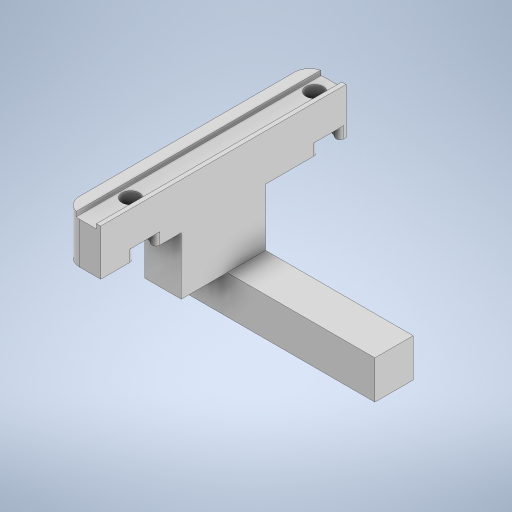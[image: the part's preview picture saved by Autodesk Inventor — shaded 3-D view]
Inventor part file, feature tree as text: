
AUTODESK INVENTOR PART (.ipt)
format: ipt  version: 2024 (Build 280153000, 153)  size: 317,952 bytes
history: native  units: in
note: dims shown in document units (in); Inventor stores cm internally (conversion verified against a paired STEP export)
features: extrude x5, sketch x5, projected_geometry x4, fillet x2
ambient origin geometry x8: Origin, YZ Plane, XZ Plane, XY Plane, X Axis, Y Axis, Z Axis, Center Point
bodies: Solid1 (feature_tree)
feature tree (16):
  extrude  "Extrusion1"  Depth=2.5197in
  extrude  "Extrusion2"  Depth=1.8898in
  extrude  "Extrusion3"  Depth=0.4724in TaperAngle=0.0deg
  fillet  "Fillet1"  Radius=0.0433in
  fillet  "Fillet2"  Radius=0.2126in
  extrude  "Extrusion15"  Depth=0.4724in TaperAngle=0.0deg
  extrude  "Extrusion18"  Depth=0.1181in TaperAngle=0.0deg
  sketch  "Sketch1"  dims[d1=0.374in d2=2.5197in]
  sketch  "Sketch2"  dims[d3=0.1772in d4=1.8898in]
  sketch  "Sketch3"  dims[d6=0.1457in d7=0.4724in d8=0.0in d9=0.0433in d10=0.2126in]
  projected_geometry  "Projected Loop2"
  projected_geometry  "Projected Loop3"
  projected_geometry  "Projected Loop4"
  projected_geometry  "Projected Loop5"
  sketch  "Sketch15"  dims[d11=0.0472in d12=0.4724in d13=0.0in]
  sketch  "Sketch27"  dims[d14=0.2953in d15=0.1181in d16=0.0in d17=0.1772in d18=0.0394in d19=0.1575in d76=0.4724in d79=0.4331in d80=0.8661in d81=0.5906in d82=0.0in d101=1.8898in d102=0.3937in d103=2.3622in d104=0.3937in d105=0.3937in d106=0.0in d42=0.0197in d43=0.0344in d44=0.0197in d45=0.0344in d46=0.0in d47=0.0in d48=0.0in d49=0.0in d50=0.0in d51=0.0in d52=0.0in d53=0.0in d55=0.0197in d56=0.0344in d57=0.0197in d58=0.0344in d60=0.0197in d61=0.0344in d62=0.0197in d63=0.0344in d72=0.0197in d73=0.0344in d74=0.0197in d75=0.0344in]
